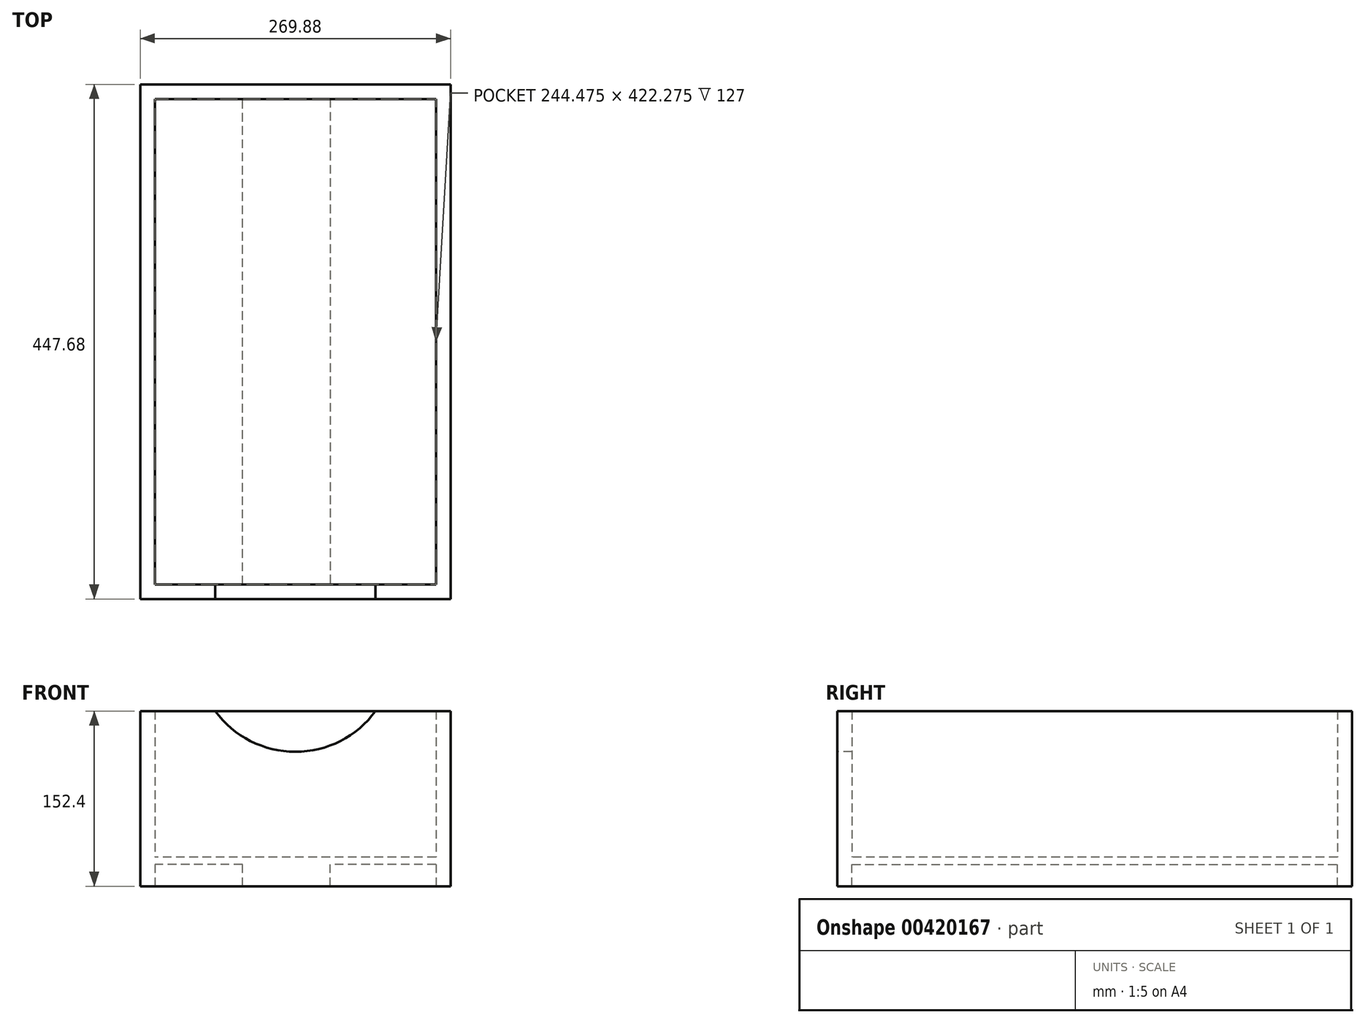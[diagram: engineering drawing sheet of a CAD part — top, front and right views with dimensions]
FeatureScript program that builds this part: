
annotation { "Feature Type Name" : "Feature", "Feature Type Description" : "" }
export const myFeature = defineFeature(function(context is Context, id is Id, definition is map)
    precondition{}
    {
        {
            var Q0;
            Q0=qCreatedBy(makeId("Top.planeOp"),FACE);
            var sketch = newSketch(context, id + "F0", { "sketchPlane" : qUnion([Q0])});
            skLineSegment(sketch, "E0.bottom", {"start": v(0, 0) * mm, "end": v(-244.47, 0) * mm});
            skLineSegment(sketch, "E0.top", {"start": v(0, -422.28) * mm, "end": v(-244.47, -422.28) * mm});
            skLineSegment(sketch, "E0.left", {"start": v(0, 0) * mm, "end": v(0, -422.28) * mm});
            skLineSegment(sketch, "E0.right", {"start": v(-244.47, 0) * mm, "end": v(-244.47, -422.28) * mm});
            skLineSegment(sketch, "E1.0", {"start": v(12.7, -434.98) * mm, "end": v(-257.17, -434.98) * mm});
            skLineSegment(sketch, "E1.1", {"start": v(12.7, 12.7) * mm, "end": v(12.7, -434.98) * mm});
            skLineSegment(sketch, "E1.2", {"start": v(12.7, 12.7) * mm, "end": v(-257.18, 12.7) * mm});
            skLineSegment(sketch, "E1.3", {"start": v(-257.18, 12.7) * mm, "end": v(-257.17, -434.98) * mm});
            skSolve(sketch);
        }
        {
            var Q0;
            Q0=makeQuery(id+"F0.imprint","IMPRINT",FACE,{"disambiguationData":[TD([[makeQuery(id+"F0.imprint","IMPRINT",EDGE,{"derivedFrom":sQuery(id+"F0.wireOp",EDGE,"E0.bottom")}),1.0]])]});
            extrude(context, id + "F1", {"entities" : qUnion([Q0]), "oppositeDirection" : true, "depth" : 6.35 * mm});
        }
        {
            var Q0;
            Q0=makeQuery(id+"F0.imprint","IMPRINT",FACE,{"disambiguationData":[TD([[makeQuery(id+"F0.imprint","IMPRINT",EDGE,{"derivedFrom":sQuery(id+"F0.wireOp",EDGE,"E0.bottom")}),-1.0]])]});
            extrude(context, id + "F2", {"entities" : qUnion([Q0]), "operationType" : NewBodyOperationType.ADD, "depth" : 127 * mm, "hasSecondDirection" : true, "secondDirectionOppositeDirection" : true, "secondDirectionDepth" : 25.4 * mm});
        }
        {
            var Q0;
            Q0=makeQuery(id+"F1.opExtrude","CAP_FACE",FACE,{"disambiguationData":[OSD([sQuery(id+"F0.wireOp",EDGE,"E0.bottom"),sQuery(id+"F0.wireOp",EDGE,"E0.top"),sQuery(id+"F0.wireOp",EDGE,"E0.left"),sQuery(id+"F0.wireOp",EDGE,"E0.right")])],"isStart":false});
            var sketch = newSketch(context, id + "F3", { "sketchPlane" : qUnion([Q0])});
            skLineSegment(sketch, "E2.bottom", {"start": v(-168.28, 422.28) * mm, "end": v(-92.08, 422.28) * mm});
            skLineSegment(sketch, "E2.top", {"start": v(-168.28, 0) * mm, "end": v(-92.07, 0) * mm});
            skLineSegment(sketch, "E2.left", {"start": v(-168.28, 422.28) * mm, "end": v(-168.28, 0) * mm});
            skLineSegment(sketch, "E2.right", {"start": v(-92.08, 422.28) * mm, "end": v(-92.07, 0) * mm});
            skSolve(sketch);
        }
        {
            var Q0;
            Q0=makeQuery(id+"F3.imprint","IMPRINT",FACE,{"disambiguationData":[TD([[makeQuery(id+"F3.imprint","IMPRINT",EDGE,{"derivedFrom":sQuery(id+"F3.wireOp",EDGE,"E2.bottom")}),1.0]])]});
            var Q1;
            Q1=makeQuery(id+"F2.opExtrude","CAP_FACE",FACE,{"disambiguationData":[OSD([sQuery(id+"F0.wireOp",EDGE,"E0.bottom"),sQuery(id+"F0.wireOp",EDGE,"E0.top"),sQuery(id+"F0.wireOp",EDGE,"E0.left"),sQuery(id+"F0.wireOp",EDGE,"E0.right"),sQuery(id+"F0.wireOp",EDGE,"E1.0"),sQuery(id+"F0.wireOp",EDGE,"E1.1"),sQuery(id+"F0.wireOp",EDGE,"E1.2"),sQuery(id+"F0.wireOp",EDGE,"E1.3")])],"isStart":true});
            extrude(context, id + "F4", {"entities" : qUnion([Q0]), "operationType" : NewBodyOperationType.ADD, "endBound" : BoundingType.UP_TO_SURFACE, "endBoundEntityFace" : qUnion([Q1]), "depth" : 25.4 * mm});
        }
        {
            var Q0;
            Q0=makeQuery(id+"F2.opExtrude","SWEPT_FACE",FACE,{"disambiguationData":[OSD([sQuery(id+"F0.wireOp",EDGE,"E1.0")])]});
            var sketch = newSketch(context, id + "F5", { "sketchPlane" : qUnion([Q0])});
            skArc(sketch, "E3", {"start": v(-206.37, 158.75) * mm, "mid": v(-122.24, 91.53) * mm, "end": v(-38.1, 158.75) * mm});
            skLineSegment(sketch, "E4", {"start": v(-206.37, 158.75) * mm, "end": v(-38.1, 158.75) * mm});
            skSolve(sketch);
        }
        {
            var Q0;
            {var subQ0=sQuery(id+"F5.wireOp",EDGE,"E4");Q0=makeQuery(id+"F5.imprint","IMPRINT",FACE,{"disambiguationData":[TD([[makeQuery(id+"F5.imprint","IMPRINT",EDGE,{"derivedFrom":subQ0}),-1.0]])]});}
            var Q1;
            {var subQ0=sQuery(id+"F5.wireOp",EDGE,"E3");var subQ1=makeQuery(id+"F2.opExtrude","CAP_EDGE",EDGE,{"disambiguationData":[OSD([sQuery(id+"F0.wireOp",EDGE,"E1.0")])],"isStart":false});var subQ2=makeQuery(id+"F5.imprint","INTERSECT",VERTEX,{"disambiguationData":[OD(0.0)],"derivedFrom":[subQ1,subQ0]});Q1=makeQuery(id+"F5.imprint","IMPRINT",FACE,{"disambiguationData":[TD([[makeQuery(id+"F5.imprint","IMPRINT",EDGE,{"disambiguationData":[TD([[subQ2,-1.0]])],"derivedFrom":subQ0}),1.0]])]});}
            extrude(context, id + "F6", {"entities" : qUnion([Q0, Q1]), "operationType" : NewBodyOperationType.REMOVE, "oppositeDirection" : true, "depth" : 25.4 * mm});
        }
    });
